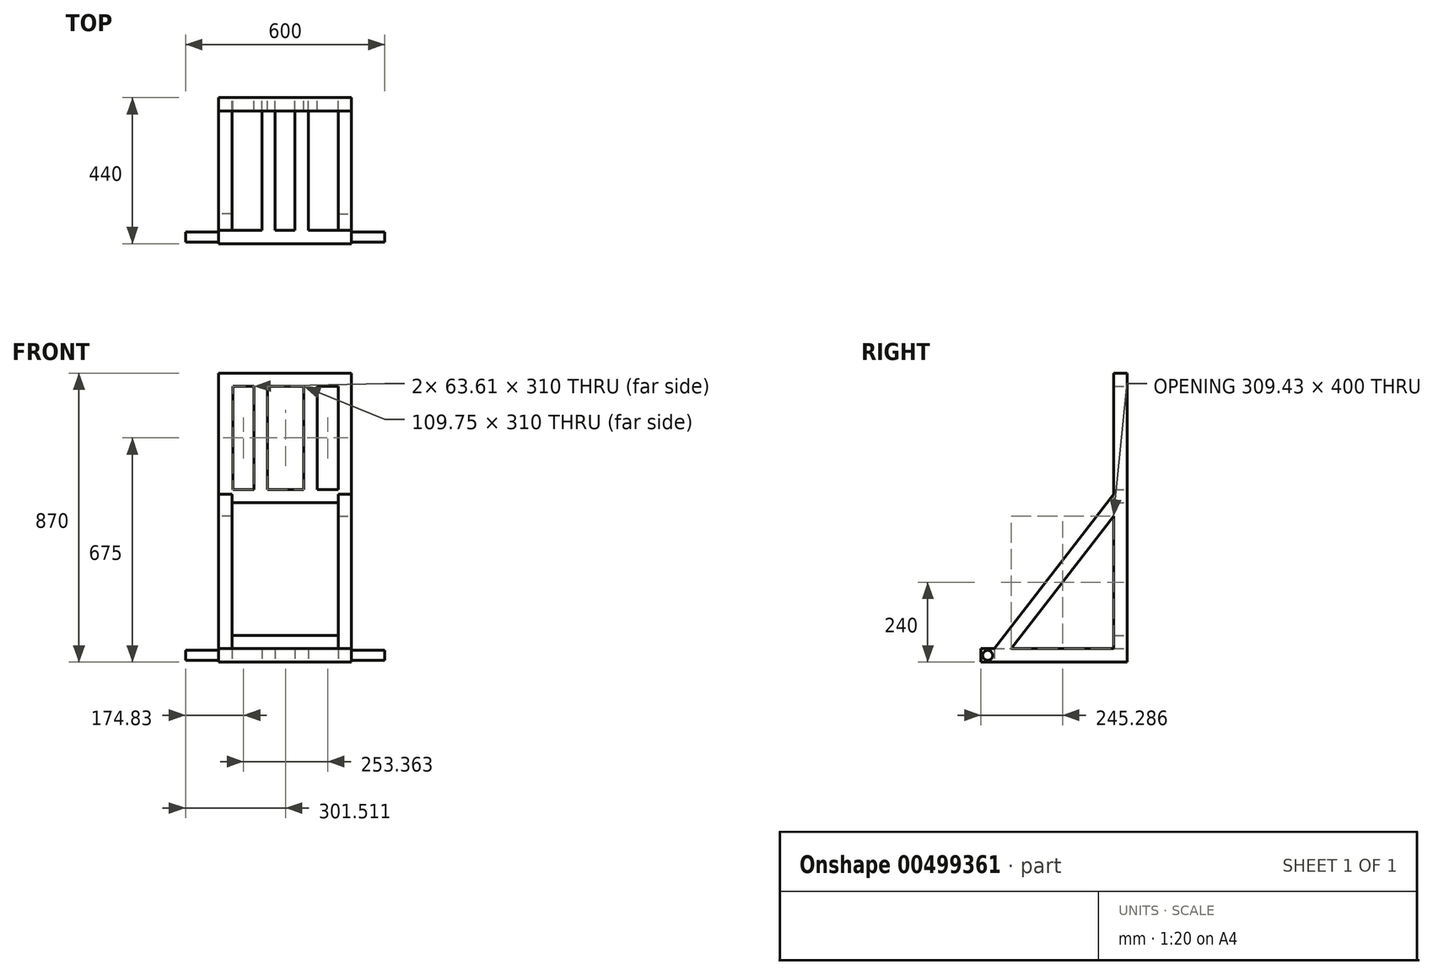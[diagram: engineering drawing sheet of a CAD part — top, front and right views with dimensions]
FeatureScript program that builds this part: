
annotation { "Feature Type Name" : "Feature", "Feature Type Description" : "" }
export const myFeature = defineFeature(function(context is Context, id is Id, definition is map)
    precondition{}
    {
        {
            var Q0;
            Q0=qCreatedBy(makeId("Front.planeOp"),FACE);
            var sketch = newSketch(context, id + "F0", { "sketchPlane" : qUnion([Q0])});
            skLineSegment(sketch, "E0", {"start": v(0, 0) * mm, "end": v(0, -830) * mm});
            skLineSegment(sketch, "E1", {"start": v(0, 0) * mm, "end": v(400, 0) * mm});
            skLineSegment(sketch, "E2", {"start": v(400, 0) * mm, "end": v(400, -830) * mm});
            skLineSegment(sketch, "E3", {"start": v(400, -830) * mm, "end": v(0, -830) * mm});
            skLineSegment(sketch, "E4.bottom", {"start": v(43.02, -40) * mm, "end": v(106.64, -40) * mm});
            skLineSegment(sketch, "E4.top", {"start": v(43.02, -350) * mm, "end": v(106.64, -350) * mm});
            skLineSegment(sketch, "E4.left", {"start": v(43.02, -40) * mm, "end": v(43.02, -350) * mm});
            skLineSegment(sketch, "E4.right", {"start": v(106.64, -40) * mm, "end": v(106.64, -350) * mm});
            skLineSegment(sketch, "E5.bottom", {"start": v(296.39, -40) * mm, "end": v(360, -40) * mm});
            skLineSegment(sketch, "E5.top", {"start": v(296.39, -350) * mm, "end": v(360, -350) * mm});
            skLineSegment(sketch, "E5.left", {"start": v(296.39, -40) * mm, "end": v(296.39, -350) * mm});
            skLineSegment(sketch, "E5.right", {"start": v(360, -40) * mm, "end": v(360, -350) * mm});
            skLineSegment(sketch, "E6.bottom", {"start": v(40, -390) * mm, "end": v(360, -390) * mm});
            skLineSegment(sketch, "E6.top", {"start": v(40, -790) * mm, "end": v(360, -790) * mm});
            skLineSegment(sketch, "E6.left", {"start": v(40, -390) * mm, "end": v(40, -790) * mm});
            skLineSegment(sketch, "E6.right", {"start": v(360, -390) * mm, "end": v(360, -790) * mm});
            skLineSegment(sketch, "E7.bottom", {"start": v(256.39, -40) * mm, "end": v(146.64, -40) * mm});
            skLineSegment(sketch, "E7.top", {"start": v(256.39, -350) * mm, "end": v(146.64, -350) * mm});
            skLineSegment(sketch, "E7.left", {"start": v(256.39, -40) * mm, "end": v(256.39, -350) * mm});
            skLineSegment(sketch, "E7.right", {"start": v(146.64, -40) * mm, "end": v(146.64, -350) * mm});
            skSolve(sketch);
        }
        {
            var Q0;
            Q0 = qSketchRegion(id + "F0", true);
            extrude(context, id + "F1", {"entities" : qUnion([Q0]), "depth" : 40 * mm});
        }
        {
            var Q0;
            Q0=qCreatedBy(makeId("Front.planeOp"),FACE);
            var sketch = newSketch(context, id + "F2", { "sketchPlane" : qUnion([Q0])});
            skLineSegment(sketch, "E8.bottom", {"start": v(400, -830) * mm, "end": v(360, -830) * mm});
            skLineSegment(sketch, "E8.top", {"start": v(400, -870) * mm, "end": v(360, -870) * mm});
            skLineSegment(sketch, "E8.left", {"start": v(400, -830) * mm, "end": v(400, -870) * mm});
            skLineSegment(sketch, "E8.right", {"start": v(360, -830) * mm, "end": v(360, -870) * mm});
            skLineSegment(sketch, "E9.bottom", {"start": v(270, -830) * mm, "end": v(230, -830) * mm});
            skLineSegment(sketch, "E9.top", {"start": v(270, -870) * mm, "end": v(230, -870) * mm});
            skLineSegment(sketch, "E9.left", {"start": v(270, -830) * mm, "end": v(270, -870) * mm});
            skLineSegment(sketch, "E9.right", {"start": v(230, -830) * mm, "end": v(230, -870) * mm});
            skLineSegment(sketch, "E10.bottom", {"start": v(130, -830) * mm, "end": v(170, -830) * mm});
            skLineSegment(sketch, "E10.top", {"start": v(130, -870) * mm, "end": v(170, -870) * mm});
            skLineSegment(sketch, "E10.left", {"start": v(130, -830) * mm, "end": v(130, -870) * mm});
            skLineSegment(sketch, "E10.right", {"start": v(170, -830) * mm, "end": v(170, -870) * mm});
            skLineSegment(sketch, "E11.bottom", {"start": v(0, -830) * mm, "end": v(40, -830) * mm});
            skLineSegment(sketch, "E11.top", {"start": v(0, -870) * mm, "end": v(40, -870) * mm});
            skLineSegment(sketch, "E11.left", {"start": v(0, -830) * mm, "end": v(0, -870) * mm});
            skLineSegment(sketch, "E11.right", {"start": v(40, -830) * mm, "end": v(40, -870) * mm});
            skSolve(sketch);
        }
        {
            var Q0;
            Q0 = qSketchRegion(id + "F2", true);
            extrude(context, id + "F3", {"entities" : qUnion([Q0]), "operationType" : NewBodyOperationType.ADD, "depth" : 400 * mm});
        }
        {
            var Q0;
            Q0=qCreatedBy(makeId("Right.planeOp"),FACE);
            var sketch = newSketch(context, id + "F4", { "sketchPlane" : qUnion([Q0])});
            skLineSegment(sketch, "E12", {"start": v(-40, -364.63) * mm, "end": v(-400, -830) * mm});
            skLineSegment(sketch, "E13", {"start": v(-349.43, -830) * mm, "end": v(-40, -430) * mm});
            skLineSegment(sketch, "E14", {"start": v(-40, -430) * mm, "end": v(-40, -364.63) * mm});
            skLineSegment(sketch, "E15", {"start": v(-349.43, -830) * mm, "end": v(-400, -830) * mm});
            skSolve(sketch);
        }
        {
            var Q0;
            Q0 = qSketchRegion(id + "F4", true);
            extrude(context, id + "F5", {"entities" : qUnion([Q0]), "operationType" : NewBodyOperationType.ADD, "depth" : 40 * mm});
        }
        {
            var Q0;
            Q0=makeQuery(id+"F3.opExtrude","CAP_FACE",FACE,{"disambiguationData":[OSD([sQuery(id+"F2.wireOp",EDGE,"E11.bottom"),sQuery(id+"F2.wireOp",EDGE,"E11.top"),sQuery(id+"F2.wireOp",EDGE,"E11.left"),sQuery(id+"F2.wireOp",EDGE,"E11.right")])],"isStart":false});
            cPlane(context, id + "F6", {"entities" : qUnion([Q0]), "cplaneType" : CPlaneType.OFFSET, "offset" : 0 * mm, "width" : 150 * mm, "height" : 150 * mm});
        }
        {
            var Q0;
            Q0=qCreatedBy(id+"F6.planeOp",FACE);
            var sketch = newSketch(context, id + "F7", { "sketchPlane" : qUnion([Q0])});
            skLineSegment(sketch, "E16.bottom", {"start": v(0, -870) * mm, "end": v(400, -870) * mm});
            skLineSegment(sketch, "E16.top", {"start": v(0, -830) * mm, "end": v(400, -830) * mm});
            skLineSegment(sketch, "E16.left", {"start": v(0, -870) * mm, "end": v(0, -830) * mm});
            skLineSegment(sketch, "E16.right", {"start": v(400, -870) * mm, "end": v(400, -830) * mm});
            skSolve(sketch);
        }
        {
            var Q0;
            Q0 = qSketchRegion(id + "F7", true);
            extrude(context, id + "F8", {"entities" : qUnion([Q0]), "operationType" : NewBodyOperationType.ADD, "depth" : 40 * mm});
        }
        {
            var Q0;
            Q0=makeQuery(id+"F8.boolean.opBoolean","MERGE",FACE,{"derivedFrom":[makeQuery(id+"F3.boolean.opBoolean","MERGE",FACE,{"derivedFrom":[makeQuery(id+"F1.opExtrude","SWEPT_FACE",FACE,{"disambiguationData":[OSD([sQuery(id+"F0.wireOp",EDGE,"E2")])]}),makeQuery(id+"F3.opExtrude","SWEPT_FACE",FACE,{"disambiguationData":[OSD([sQuery(id+"F2.wireOp",EDGE,"E8.left")])]})]}),makeQuery(id+"F8.opExtrude","SWEPT_FACE",FACE,{"disambiguationData":[OSD([sQuery(id+"F7.wireOp",EDGE,"E16.right")])]})]});
            cPlane(context, id + "F9", {"entities" : qUnion([Q0]), "cplaneType" : CPlaneType.OFFSET, "offset" : 0 * mm, "width" : 150 * mm, "height" : 150 * mm});
        }
        {
            var Q0;
            Q0=qCreatedBy(id+"F9.planeOp",FACE);
            var sketch = newSketch(context, id + "F10", { "sketchPlane" : qUnion([Q0])});
            skLineSegment(sketch, "E17", {"start": v(-349.43, -830) * mm, "end": v(-40, -430) * mm});
            skLineSegment(sketch, "E18", {"start": v(-40, -364.63) * mm, "end": v(-400, -830) * mm});
            skLineSegment(sketch, "E19", {"start": v(-349.43, -830) * mm, "end": v(-400, -830) * mm});
            skLineSegment(sketch, "E20", {"start": v(-40, -430) * mm, "end": v(-40, -364.63) * mm});
            skSolve(sketch);
        }
        {
            var Q0;
            Q0 = qSketchRegion(id + "F10", true);
            extrude(context, id + "F11", {"entities" : qUnion([Q0]), "operationType" : NewBodyOperationType.ADD, "oppositeDirection" : true, "depth" : 40 * mm});
        }
        {
            var Q0;
            Q0=qCreatedBy(id+"F9.planeOp",FACE);
            var sketch = newSketch(context, id + "F12", { "sketchPlane" : qUnion([Q0])});
            skCircle(sketch, "E21", {"center": v(-420, -850) * mm, "radius": 15 * mm});
            skSolve(sketch);
        }
        {
            var Q0;
            Q0 = qSketchRegion(id + "F12", true);
            extrude(context, id + "F13", {"entities" : qUnion([Q0]), "operationType" : NewBodyOperationType.ADD, "depth" : 100 * mm});
        }
        {
            var Q0;
            Q0=qCreatedBy(makeId("Right.planeOp"),FACE);
            var sketch = newSketch(context, id + "F14", { "sketchPlane" : qUnion([Q0])});
            skCircle(sketch, "E22", {"center": v(-420, -850) * mm, "radius": 15 * mm});
            skSolve(sketch);
        }
        {
            var Q0;
            Q0 = qSketchRegion(id + "F14", true);
            extrude(context, id + "F15", {"entities" : qUnion([Q0]), "operationType" : NewBodyOperationType.ADD, "oppositeDirection" : true, "depth" : 100 * mm});
        }
    });
